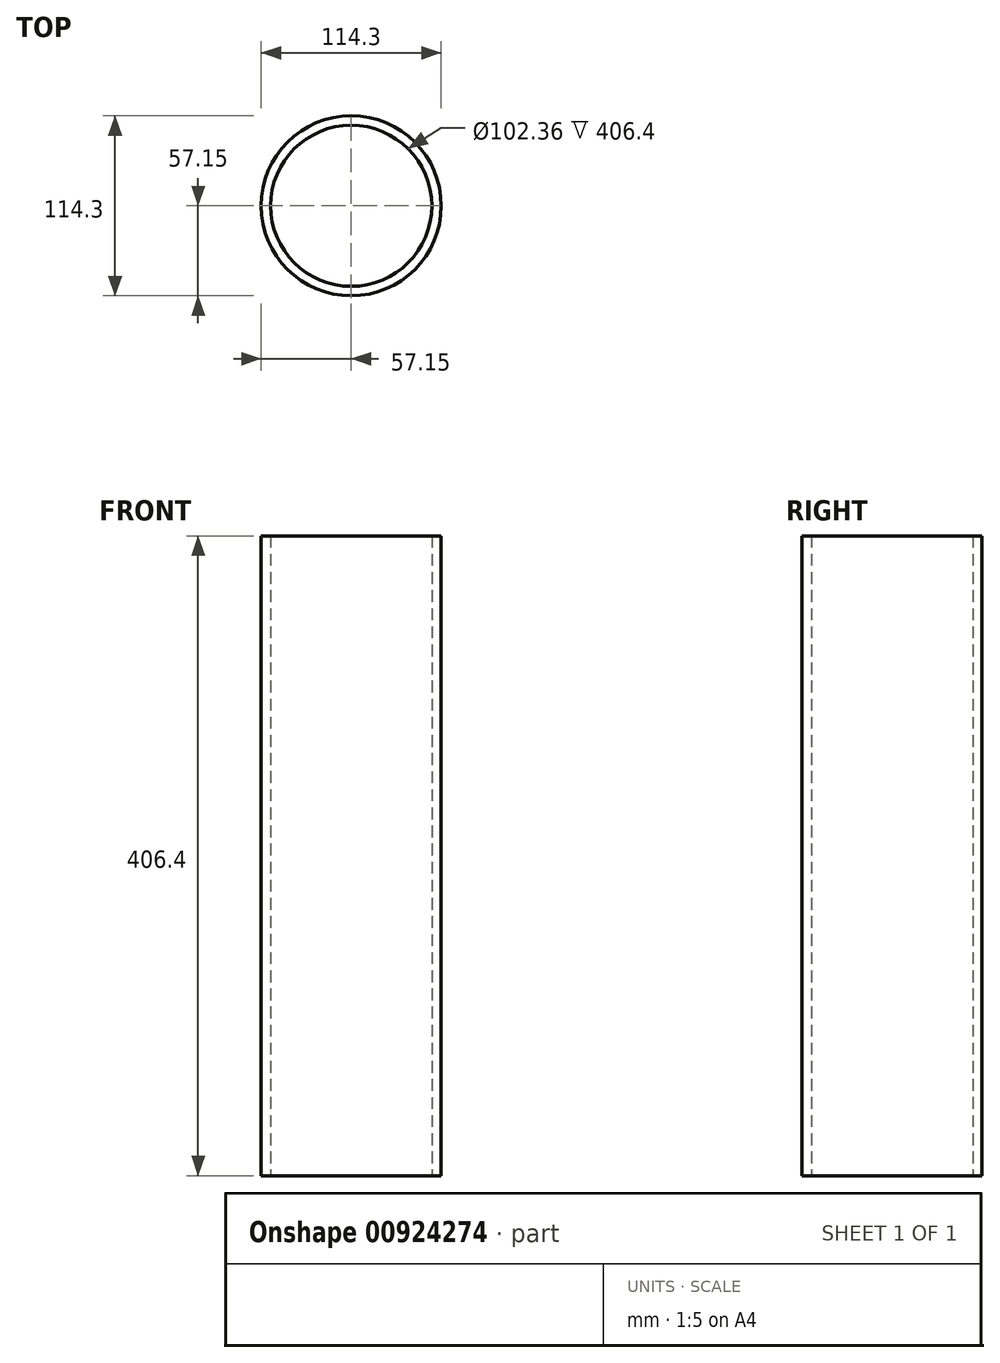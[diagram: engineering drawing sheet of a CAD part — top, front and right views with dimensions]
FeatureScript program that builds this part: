
annotation { "Feature Type Name" : "Feature", "Feature Type Description" : "" }
export const myFeature = defineFeature(function(context is Context, id is Id, definition is map)
    precondition{}
    {
        {
            var Q0;
            Q0=qCreatedBy(makeId("Top.planeOp"),FACE);
            var sketch = newSketch(context, id + "F0", { "sketchPlane" : qUnion([Q0])});
            skCircle(sketch, "E0", {"center": v(0, 0) * mm, "radius": 57.15 * mm});
            skCircle(sketch, "E1", {"center": v(0, 0) * mm, "radius": 51.18 * mm});
            skSolve(sketch);
        }
        {
            var Q0;
            Q0=makeQuery(id+"F0.imprint","IMPRINT",FACE,{"disambiguationData":[TD([[makeQuery(id+"F0.imprint","IMPRINT",EDGE,{"derivedFrom":sQuery(id+"F0.wireOp",EDGE,"E0")}),1.0]])]});
            extrude(context, id + "F1", {"entities" : qUnion([Q0]), "depth" : 406.4 * mm, "offsetDistance" : 25.4 * mm});
        }
    });
